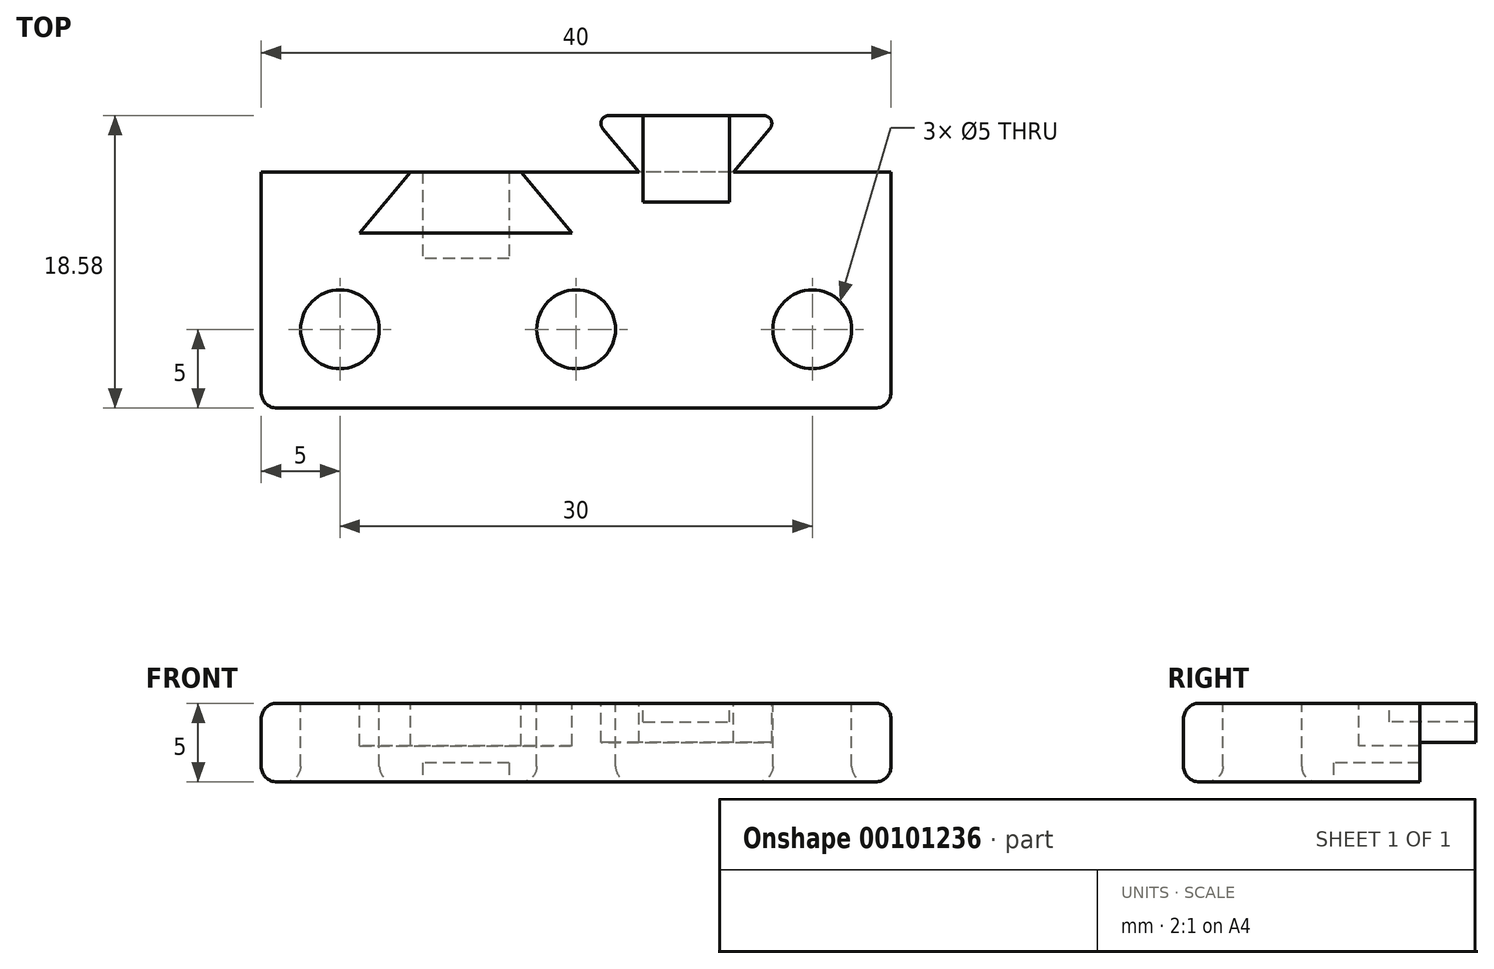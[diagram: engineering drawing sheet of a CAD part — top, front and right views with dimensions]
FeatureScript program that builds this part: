
annotation { "Feature Type Name" : "Feature", "Feature Type Description" : "" }
export const myFeature = defineFeature(function(context is Context, id is Id, definition is map)
    precondition{}
    {
        {
            var Q0;
            Q0=qCreatedBy(makeId("Top.planeOp"),FACE);
            var sketch = newSketch(context, id + "F0", { "sketchPlane" : qUnion([Q0])});
            skLineSegment(sketch, "E0", {"start": v(0, 0) * mm, "end": v(40, 0) * mm});
            skLineSegment(sketch, "E1", {"start": v(40, 0) * mm, "end": v(40, 15) * mm});
            skLineSegment(sketch, "E2", {"start": v(40, 15) * mm, "end": v(0, 15) * mm});
            skLineSegment(sketch, "E3", {"start": v(0, 15) * mm, "end": v(0, 0) * mm});
            skSolve(sketch);
        }
        {
            var Q0;
            Q0 = qSketchRegion(id + "F0", true);
            extrude(context, id + "F1", {"entities" : qUnion([Q0]), "depth" : 5 * mm});
        }
        {
            var Q0;
            Q0=makeQuery(id+"F1.opExtrude","CAP_FACE",FACE,{"disambiguationData":[OSD([sQuery(id+"F0.wireOp",EDGE,"E0"),sQuery(id+"F0.wireOp",EDGE,"E1"),sQuery(id+"F0.wireOp",EDGE,"E2"),sQuery(id+"F0.wireOp",EDGE,"E3")])],"isStart":false});
            var sketch = newSketch(context, id + "F2", { "sketchPlane" : qUnion([Q0])});
            skCircle(sketch, "E4", {"center": v(5, 5) * mm, "radius": 2.5 * mm});
            skCircle(sketch, "E5", {"center": v(20, 5) * mm, "radius": 2.5 * mm});
            skCircle(sketch, "E6", {"center": v(35, 5) * mm, "radius": 2.5 * mm});
            skSolve(sketch);
        }
        {
            var Q0;
            Q0 = qSketchRegion(id + "F2", true);
            extrude(context, id + "F3", {"entities" : qUnion([Q0]), "operationType" : NewBodyOperationType.REMOVE, "endBound" : BoundingType.THROUGH_ALL, "oppositeDirection" : true, "depth" : 25 * mm});
        }
        {
            var Q0;
            Q0=makeQuery(id+"F1.opExtrude","CAP_FACE",FACE,{"disambiguationData":[OSD([sQuery(id+"F0.wireOp",EDGE,"E0"),sQuery(id+"F0.wireOp",EDGE,"E1"),sQuery(id+"F0.wireOp",EDGE,"E2"),sQuery(id+"F0.wireOp",EDGE,"E3")])],"isStart":false});
            var sketch = newSketch(context, id + "F4", { "sketchPlane" : qUnion([Q0])});
            skLineSegment(sketch, "E7", {"start": v(24, 15) * mm, "end": v(21, 18.58) * mm});
            skLineSegment(sketch, "E8", {"start": v(21, 18.58) * mm, "end": v(33, 18.58) * mm});
            skLineSegment(sketch, "E9", {"start": v(33, 18.58) * mm, "end": v(30, 15) * mm});
            skLineSegment(sketch, "E10", {"start": v(30, 15) * mm, "end": v(24, 15) * mm});
            skSolve(sketch);
        }
        {
            var Q0;
            Q0 = qSketchRegion(id + "F4", true);
            extrude(context, id + "F5", {"entities" : qUnion([Q0]), "operationType" : NewBodyOperationType.ADD, "oppositeDirection" : true, "depth" : 2.5 * mm});
        }
        {
            var Q0;
            Q0=makeQuery(id+"F5.boolean.opBoolean","MERGE",FACE,{"derivedFrom":[makeQuery(id+"F1.opExtrude","CAP_FACE",FACE,{"disambiguationData":[OSD([sQuery(id+"F0.wireOp",EDGE,"E0"),sQuery(id+"F0.wireOp",EDGE,"E1"),sQuery(id+"F0.wireOp",EDGE,"E2"),sQuery(id+"F0.wireOp",EDGE,"E3")])],"isStart":false}),makeQuery(id+"F5.opExtrude","CAP_FACE",FACE,{"disambiguationData":[OSD([sQuery(id+"F4.wireOp",EDGE,"E7"),sQuery(id+"F4.wireOp",EDGE,"E8"),sQuery(id+"F4.wireOp",EDGE,"E9"),sQuery(id+"F4.wireOp",EDGE,"E10")])],"isStart":true})]});
            var sketch = newSketch(context, id + "F6", { "sketchPlane" : qUnion([Q0])});
            skLineSegment(sketch, "E11", {"start": v(9.5, 15) * mm, "end": v(6.25, 11.13) * mm});
            skLineSegment(sketch, "E12", {"start": v(6.25, 11.13) * mm, "end": v(19.75, 11.13) * mm});
            skLineSegment(sketch, "E13", {"start": v(19.75, 11.13) * mm, "end": v(16.5, 15) * mm});
            skLineSegment(sketch, "E14", {"start": v(16.5, 15) * mm, "end": v(9.5, 15) * mm});
            skSolve(sketch);
        }
        {
            var Q0;
            Q0 = qSketchRegion(id + "F6", true);
            extrude(context, id + "F7", {"entities" : qUnion([Q0]), "operationType" : NewBodyOperationType.REMOVE, "oppositeDirection" : true, "depth" : 2.7 * mm});
        }
        {
            var Q0;
            Q0=makeQuery(id+"F1.opExtrude","SWEPT_EDGE",EDGE,{"disambiguationData":[OSD([sQuery(id+"F0.wireOp",EDGE,"E0"),sQuery(id+"F0.wireOp",EDGE,"E3")])]});
            var Q1;
            Q1=makeQuery(id+"F1.opExtrude","SWEPT_EDGE",EDGE,{"disambiguationData":[OSD([sQuery(id+"F0.wireOp",EDGE,"E0"),sQuery(id+"F0.wireOp",EDGE,"E1")])]});
            var Q2;
            Q2=makeQuery(id+"F1.opExtrude","CAP_EDGE",EDGE,{"disambiguationData":[OSD([sQuery(id+"F0.wireOp",EDGE,"E3")])],"isStart":false});
            var Q3;
            Q3=makeQuery(id+"F1.opExtrude","CAP_EDGE",EDGE,{"disambiguationData":[OSD([sQuery(id+"F0.wireOp",EDGE,"E3")])],"isStart":true});
            var Q4;
            Q4=makeQuery(id+"F1.opExtrude","CAP_EDGE",EDGE,{"disambiguationData":[OSD([sQuery(id+"F0.wireOp",EDGE,"E1")])],"isStart":false});
            var Q5;
            Q5=makeQuery(id+"F1.opExtrude","CAP_EDGE",EDGE,{"disambiguationData":[OSD([sQuery(id+"F0.wireOp",EDGE,"E1")])],"isStart":true});
            var Q6;
            Q6=makeQuery(id+"F1.opExtrude","CAP_EDGE",EDGE,{"disambiguationData":[OSD([sQuery(id+"F0.wireOp",EDGE,"E0")])],"isStart":false});
            var Q7;
            Q7=makeQuery(id+"F1.opExtrude","CAP_EDGE",EDGE,{"disambiguationData":[OSD([sQuery(id+"F0.wireOp",EDGE,"E0")])],"isStart":true});
            fillet(context, id + "F8", {"entities" : qUnion([Q0, Q1, Q2, Q3, Q4, Q5, Q6, Q7]), "radius" : 1 * mm, "tangentPropagation" : true, "allowEdgeOverflow" : false});
        }
        {
            var Q0;
            Q0=makeQuery(id+"F3.boolean.opBoolean","COPY",EDGE,{"derivedFrom":makeQuery(id+"F3.opExtrude","CAP_EDGE",EDGE,{"disambiguationData":[OSD([sQuery(id+"F2.wireOp",EDGE,"E4")])],"isStart":true})});
            var Q1;
            Q1=makeQuery(id+"F3.boolean.opBoolean","COPY",EDGE,{"derivedFrom":makeQuery(id+"F3.opExtrude","CAP_EDGE",EDGE,{"disambiguationData":[OSD([sQuery(id+"F2.wireOp",EDGE,"E5")])],"isStart":true})});
            var Q2;
            Q2=makeQuery(id+"F3.boolean.opBoolean","COPY",EDGE,{"derivedFrom":makeQuery(id+"F3.opExtrude","CAP_EDGE",EDGE,{"disambiguationData":[OSD([sQuery(id+"F2.wireOp",EDGE,"E6")])],"isStart":true})});
            var Q3;
            Q3=makeQuery(id+"F3.boolean.opBoolean","INTERSECT",EDGE,{"derivedFrom":[makeQuery(id+"F1.opExtrude","CAP_FACE",FACE,{"disambiguationData":[OSD([sQuery(id+"F0.wireOp",EDGE,"E0"),sQuery(id+"F0.wireOp",EDGE,"E1"),sQuery(id+"F0.wireOp",EDGE,"E2"),sQuery(id+"F0.wireOp",EDGE,"E3")])],"isStart":true}),makeQuery(id+"F3.opExtrude","SWEPT_FACE",FACE,{"disambiguationData":[OSD([sQuery(id+"F2.wireOp",EDGE,"E4")])]})]});
            var Q4;
            Q4=makeQuery(id+"F3.boolean.opBoolean","INTERSECT",EDGE,{"derivedFrom":[makeQuery(id+"F1.opExtrude","CAP_FACE",FACE,{"disambiguationData":[OSD([sQuery(id+"F0.wireOp",EDGE,"E0"),sQuery(id+"F0.wireOp",EDGE,"E1"),sQuery(id+"F0.wireOp",EDGE,"E2"),sQuery(id+"F0.wireOp",EDGE,"E3")])],"isStart":true}),makeQuery(id+"F3.opExtrude","SWEPT_FACE",FACE,{"disambiguationData":[OSD([sQuery(id+"F2.wireOp",EDGE,"E5")])]})]});
            var Q5;
            Q5=makeQuery(id+"F3.boolean.opBoolean","INTERSECT",EDGE,{"derivedFrom":[makeQuery(id+"F1.opExtrude","CAP_FACE",FACE,{"disambiguationData":[OSD([sQuery(id+"F0.wireOp",EDGE,"E0"),sQuery(id+"F0.wireOp",EDGE,"E1"),sQuery(id+"F0.wireOp",EDGE,"E2"),sQuery(id+"F0.wireOp",EDGE,"E3")])],"isStart":true}),makeQuery(id+"F3.opExtrude","SWEPT_FACE",FACE,{"disambiguationData":[OSD([sQuery(id+"F2.wireOp",EDGE,"E6")])]})]});
            fillet(context, id + "F9", {"entities" : qUnion([Q0, Q1, Q2, Q3, Q4, Q5]), "radius" : 1 * mm, "tangentPropagation" : true, "allowEdgeOverflow" : false});
        }
        {
            var Q0;
            Q0=makeQuery(id+"F5.opExtrude","SWEPT_EDGE",EDGE,{"disambiguationData":[OSD([sQuery(id+"F4.wireOp",EDGE,"E7"),sQuery(id+"F4.wireOp",EDGE,"E8")])]});
            var Q1;
            Q1=makeQuery(id+"F5.opExtrude","SWEPT_EDGE",EDGE,{"disambiguationData":[OSD([sQuery(id+"F4.wireOp",EDGE,"E8"),sQuery(id+"F4.wireOp",EDGE,"E9")])]});
            var Q2;
            Q2=makeQuery(id+"F7.boolean.opBoolean","COPY",EDGE,{"derivedFrom":makeQuery(id+"F7.opExtrude","SWEPT_EDGE",EDGE,{"disambiguationData":[OSD([sQuery(id+"F0.wireOp",EDGE,"E2"),sQuery(id+"F6.wireOp",EDGE,"E11"),sQuery(id+"F6.wireOp",EDGE,"E14")])]})});
            var Q3;
            Q3=makeQuery(id+"F7.boolean.opBoolean","COPY",EDGE,{"derivedFrom":makeQuery(id+"F7.opExtrude","SWEPT_EDGE",EDGE,{"disambiguationData":[OSD([sQuery(id+"F0.wireOp",EDGE,"E2"),sQuery(id+"F6.wireOp",EDGE,"E13"),sQuery(id+"F6.wireOp",EDGE,"E14")])]})});
            fillet(context, id + "F10", {"entities" : qUnion([Q0, Q1, Q2, Q3]), "radius" : 0.5 * mm, "tangentPropagation" : true, "allowEdgeOverflow" : false});
        }
        {
            var Q0;
            Q0=makeQuery(id+"F5.boolean.opBoolean","MERGE",FACE,{"derivedFrom":[makeQuery(id+"F1.opExtrude","CAP_FACE",FACE,{"disambiguationData":[OSD([sQuery(id+"F0.wireOp",EDGE,"E0"),sQuery(id+"F0.wireOp",EDGE,"E1"),sQuery(id+"F0.wireOp",EDGE,"E2"),sQuery(id+"F0.wireOp",EDGE,"E3")])],"isStart":false}),makeQuery(id+"F5.opExtrude","CAP_FACE",FACE,{"disambiguationData":[OSD([sQuery(id+"F4.wireOp",EDGE,"E7"),sQuery(id+"F4.wireOp",EDGE,"E8"),sQuery(id+"F4.wireOp",EDGE,"E9"),sQuery(id+"F4.wireOp",EDGE,"E10")])],"isStart":true})]});
            var sketch = newSketch(context, id + "F11", { "sketchPlane" : qUnion([Q0])});
            skLineSegment(sketch, "E15.bottom", {"start": v(24.25, 18.58) * mm, "end": v(29.75, 18.58) * mm});
            skLineSegment(sketch, "E15.top", {"start": v(24.25, 13.08) * mm, "end": v(29.75, 13.08) * mm});
            skLineSegment(sketch, "E15.left", {"start": v(24.25, 18.58) * mm, "end": v(24.25, 13.08) * mm});
            skLineSegment(sketch, "E15.right", {"start": v(29.75, 18.58) * mm, "end": v(29.75, 13.08) * mm});
            skSolve(sketch);
        }
        {
            var Q0;
            Q0 = qSketchRegion(id + "F11", true);
            extrude(context, id + "F12", {"entities" : qUnion([Q0]), "operationType" : NewBodyOperationType.REMOVE, "oppositeDirection" : true, "depth" : 1.2 * mm});
        }
        {
            var Q0;
            Q0=makeQuery(id+"F1.opExtrude","CAP_FACE",FACE,{"disambiguationData":[OSD([sQuery(id+"F0.wireOp",EDGE,"E0"),sQuery(id+"F0.wireOp",EDGE,"E1"),sQuery(id+"F0.wireOp",EDGE,"E2"),sQuery(id+"F0.wireOp",EDGE,"E3")])],"isStart":true});
            var sketch = newSketch(context, id + "F13", { "sketchPlane" : qUnion([Q0])});
            skLineSegment(sketch, "E16.bottom", {"start": v(15.75, -15) * mm, "end": v(10.25, -15) * mm});
            skLineSegment(sketch, "E16.top", {"start": v(15.75, -9.5) * mm, "end": v(10.25, -9.5) * mm});
            skLineSegment(sketch, "E16.left", {"start": v(15.75, -15) * mm, "end": v(15.75, -9.5) * mm});
            skLineSegment(sketch, "E16.right", {"start": v(10.25, -15) * mm, "end": v(10.25, -9.5) * mm});
            skSolve(sketch);
        }
        {
            var Q0;
            Q0 = qSketchRegion(id + "F13", true);
            extrude(context, id + "F14", {"entities" : qUnion([Q0]), "operationType" : NewBodyOperationType.REMOVE, "oppositeDirection" : true, "depth" : 1.2 * mm});
        }
    });
